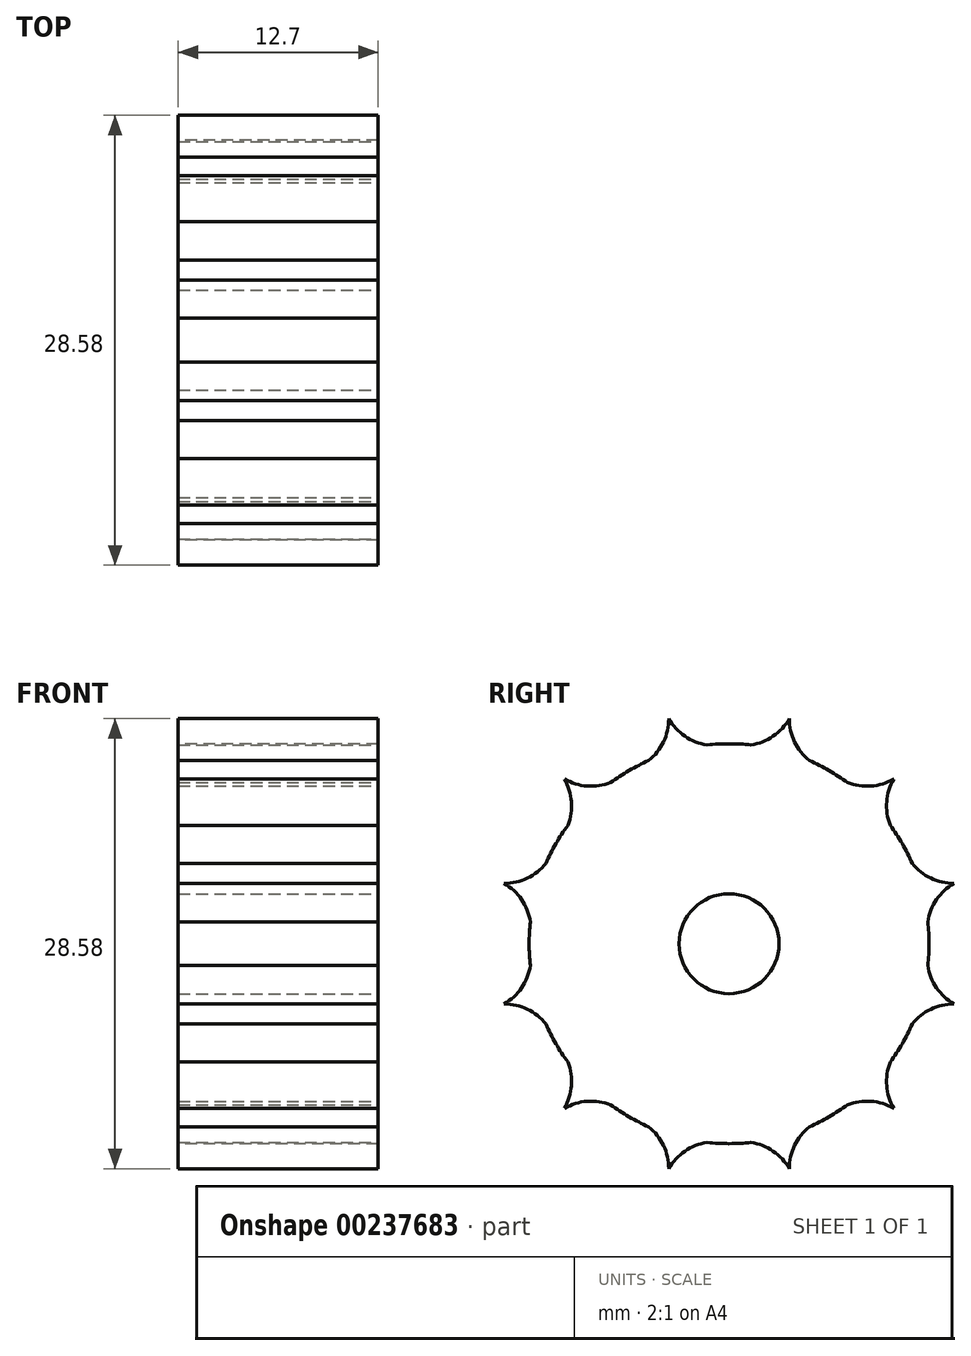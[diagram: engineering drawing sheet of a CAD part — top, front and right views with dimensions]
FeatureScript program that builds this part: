
annotation { "Feature Type Name" : "Feature", "Feature Type Description" : "" }
export const myFeature = defineFeature(function(context is Context, id is Id, definition is map)
    precondition{}
    {
        {
            var Q0;
            Q0=qCreatedBy(makeId("Right.planeOp"),FACE);
            var sketch = newSketch(context, id + "F0", { "sketchPlane" : qUnion([Q0])});
            skCircle(sketch, "E0", {"center": v(0, 0) * mm, "radius": 3.18 * mm});
            skCircle(sketch, "E1", {"center": v(0, 0) * mm, "radius": 12.7 * mm});
            skSolve(sketch);
        }
        {
            var Q0;
            Q0=makeQuery(id+"F0.imprint","IMPRINT",FACE,{"disambiguationData":[TD([[makeQuery(id+"F0.imprint","IMPRINT",EDGE,{"derivedFrom":sQuery(id+"F0.wireOp",EDGE,"E0")}),-1.0]])]});
            extrude(context, id + "F1", {"entities" : qUnion([Q0]), "depth" : 12.7 * mm});
        }
        {
            var Q0;
            Q0=makeQuery(id+"F1.opExtrude","CAP_FACE",FACE,{"disambiguationData":[OSD([sQuery(id+"F0.wireOp",EDGE,"E0"),sQuery(id+"F0.wireOp",EDGE,"E1")])],"isStart":false});
            var sketch = newSketch(context, id + "F2", { "sketchPlane" : qUnion([Q0])});
            skLineSegment(sketch, "E2", {"start": v(0, 0) * mm, "end": v(0, 12.7) * mm});
            skCircle(sketch, "E3.cCircle", {"center": v(0, 0) * mm, "radius": 12.7 * mm, "construction": true});
            skLineSegment(sketch, "E3.0", {"start": v(0, 12.7) * mm, "end": v(6.35, 11) * mm});
            skLineSegment(sketch, "E3.1", {"start": v(6.35, 11) * mm, "end": v(11, 6.35) * mm});
            skLineSegment(sketch, "E3.2", {"start": v(11, 6.35) * mm, "end": v(12.7, 0) * mm});
            skLineSegment(sketch, "E3.3", {"start": v(12.7, 0) * mm, "end": v(11, -6.35) * mm});
            skLineSegment(sketch, "E3.4", {"start": v(11, -6.35) * mm, "end": v(6.35, -11) * mm});
            skLineSegment(sketch, "E3.5", {"start": v(6.35, -11) * mm, "end": v(0, -12.7) * mm});
            skLineSegment(sketch, "E3.6", {"start": v(0, -12.7) * mm, "end": v(-6.35, -11) * mm});
            skLineSegment(sketch, "E3.7", {"start": v(-6.35, -11) * mm, "end": v(-11, -6.35) * mm});
            skLineSegment(sketch, "E3.8", {"start": v(-11, -6.35) * mm, "end": v(-12.7, 0) * mm});
            skLineSegment(sketch, "E3.9", {"start": v(-12.7, 0) * mm, "end": v(-11, 6.35) * mm});
            skLineSegment(sketch, "E3.10", {"start": v(-11, 6.35) * mm, "end": v(-6.35, 11) * mm});
            skLineSegment(sketch, "E3.11", {"start": v(-6.35, 11) * mm, "end": v(0, 12.7) * mm});
            skPoint(sketch, "E4.start.orphan", {"position": v(3.17, 11.85) * mm});
            skArc(sketch, "E5", {"start": v(3.83, 14.3) * mm, "mid": v(4.53, 12.22) * mm, "end": v(6.35, 11) * mm});
            skArc(sketch, "E6", {"start": v(0, 12.7) * mm, "mid": v(2.19, 12.84) * mm, "end": v(3.83, 14.3) * mm});
            skArc(sketch, "E7.1.0", {"start": v(-3.83, 14.3) * mm, "mid": v(-2.19, 12.84) * mm, "end": v(0, 12.7) * mm});
            skArc(sketch, "E7.1.1", {"start": v(-6.35, 11) * mm, "mid": v(-4.53, 12.22) * mm, "end": v(-3.83, 14.3) * mm});
            skArc(sketch, "E7.2.0", {"start": v(-10.46, 10.46) * mm, "mid": v(-8.32, 10.03) * mm, "end": v(-6.35, 11) * mm});
            skArc(sketch, "E7.2.1", {"start": v(-11, 6.35) * mm, "mid": v(-10.03, 8.32) * mm, "end": v(-10.46, 10.46) * mm});
            skArc(sketch, "E7.3.0", {"start": v(-14.3, 3.83) * mm, "mid": v(-12.22, 4.53) * mm, "end": v(-11, 6.35) * mm});
            skArc(sketch, "E7.3.1", {"start": v(-12.7, 0) * mm, "mid": v(-12.84, 2.19) * mm, "end": v(-14.3, 3.83) * mm});
            skArc(sketch, "E7.4.0", {"start": v(-14.3, -3.83) * mm, "mid": v(-12.84, -2.19) * mm, "end": v(-12.7, 0) * mm});
            skArc(sketch, "E7.4.1", {"start": v(-11, -6.35) * mm, "mid": v(-12.22, -4.53) * mm, "end": v(-14.3, -3.83) * mm});
            skArc(sketch, "E7.5.0", {"start": v(-10.46, -10.46) * mm, "mid": v(-10.03, -8.32) * mm, "end": v(-11, -6.35) * mm});
            skArc(sketch, "E7.5.1", {"start": v(-6.35, -11) * mm, "mid": v(-8.32, -10.03) * mm, "end": v(-10.46, -10.46) * mm});
            skArc(sketch, "E7.6.0", {"start": v(-3.83, -14.3) * mm, "mid": v(-4.53, -12.22) * mm, "end": v(-6.35, -11) * mm});
            skArc(sketch, "E7.6.1", {"start": v(0, -12.7) * mm, "mid": v(-2.19, -12.84) * mm, "end": v(-3.83, -14.3) * mm});
            skArc(sketch, "E7.7.0", {"start": v(3.83, -14.3) * mm, "mid": v(2.19, -12.84) * mm, "end": v(0, -12.7) * mm});
            skArc(sketch, "E7.7.1", {"start": v(6.35, -11) * mm, "mid": v(4.53, -12.22) * mm, "end": v(3.83, -14.3) * mm});
            skArc(sketch, "E7.8.0", {"start": v(10.46, -10.46) * mm, "mid": v(8.32, -10.03) * mm, "end": v(6.35, -11) * mm});
            skArc(sketch, "E7.8.1", {"start": v(11, -6.35) * mm, "mid": v(10.03, -8.32) * mm, "end": v(10.46, -10.46) * mm});
            skArc(sketch, "E7.9.0", {"start": v(14.3, -3.83) * mm, "mid": v(12.22, -4.53) * mm, "end": v(11, -6.35) * mm});
            skArc(sketch, "E7.9.1", {"start": v(12.7, 0) * mm, "mid": v(12.84, -2.19) * mm, "end": v(14.3, -3.83) * mm});
            skArc(sketch, "E7.10.0", {"start": v(14.3, 3.83) * mm, "mid": v(12.84, 2.19) * mm, "end": v(12.7, 0) * mm});
            skArc(sketch, "E7.10.1", {"start": v(11, 6.35) * mm, "mid": v(12.22, 4.53) * mm, "end": v(14.3, 3.83) * mm});
            skArc(sketch, "E7.11.0", {"start": v(10.46, 10.46) * mm, "mid": v(10.03, 8.32) * mm, "end": v(11, 6.35) * mm});
            skArc(sketch, "E7.11.1", {"start": v(6.35, 11) * mm, "mid": v(8.32, 10.03) * mm, "end": v(10.46, 10.46) * mm});
            skSolve(sketch);
        }
        {
            var Q0;
            Q0 = qSketchRegion(id + "F2", true);
            extrude(context, id + "F3", {"entities" : qUnion([Q0]), "operationType" : NewBodyOperationType.ADD, "oppositeDirection" : true, "depth" : 12.7 * mm});
        }
        {
            var Q0;
            Q0=makeQuery(id+"F3.boolean.opBoolean","MERGE",FACE,{"derivedFrom":[makeQuery(id+"F1.opExtrude","CAP_FACE",FACE,{"disambiguationData":[OSD([sQuery(id+"F0.wireOp",EDGE,"E0"),sQuery(id+"F0.wireOp",EDGE,"E1")])],"isStart":false}),makeQuery(id+"F3.opExtrude","CAP_FACE",FACE,{"disambiguationData":[OSD([sQuery(id+"F2.wireOp",EDGE,"E5"),sQuery(id+"F2.wireOp",EDGE,"E6"),sQuery(id+"F2.wireOp",EDGE,"E7.1.0"),sQuery(id+"F2.wireOp",EDGE,"E7.1.1"),sQuery(id+"F2.wireOp",EDGE,"E7.2.0"),sQuery(id+"F2.wireOp",EDGE,"E7.2.1"),sQuery(id+"F2.wireOp",EDGE,"E7.3.0"),sQuery(id+"F2.wireOp",EDGE,"E7.3.1"),sQuery(id+"F2.wireOp",EDGE,"E7.4.0"),sQuery(id+"F2.wireOp",EDGE,"E7.4.1"),sQuery(id+"F2.wireOp",EDGE,"E7.5.0"),sQuery(id+"F2.wireOp",EDGE,"E7.5.1"),sQuery(id+"F2.wireOp",EDGE,"E7.6.0"),sQuery(id+"F2.wireOp",EDGE,"E7.6.1"),sQuery(id+"F2.wireOp",EDGE,"E7.7.0"),sQuery(id+"F2.wireOp",EDGE,"E7.7.1"),sQuery(id+"F2.wireOp",EDGE,"E7.8.0"),sQuery(id+"F2.wireOp",EDGE,"E7.8.1"),sQuery(id+"F2.wireOp",EDGE,"E7.9.0"),sQuery(id+"F2.wireOp",EDGE,"E7.9.1"),sQuery(id+"F2.wireOp",EDGE,"E7.10.0"),sQuery(id+"F2.wireOp",EDGE,"E7.10.1"),sQuery(id+"F2.wireOp",EDGE,"E7.11.0"),sQuery(id+"F2.wireOp",EDGE,"E7.11.1")])],"isStart":true})]});
            var sketch = newSketch(context, id + "F4", { "sketchPlane" : qUnion([Q0])});
            skPoint(sketch, "E8", {"position": v(0, 0) * mm});
            skSolve(sketch);
        }
        {
            var Q0;
            Q0=sQuery(id+"F4.wireOp",VERTEX,"E8");
            var Q1;
            Q1=makeQuery(id+"F1.opExtrude","SWEPT_BODY",BODY,{"disambiguationData":[OSD([sQuery(id+"F0.wireOp",EDGE,"E0"),sQuery(id+"F0.wireOp",EDGE,"E1")])]});
            hole(context, id + "F5", {"style" : HoleStyle.SIMPLE, "endStyle" : HoleEndStyle.THROUGH, "holeDiameter" : 6.35 * mm, "locations" : qUnion([Q0]), "scope" : qUnion([Q1]), "isTappedThrough" : true});
        }
    });
